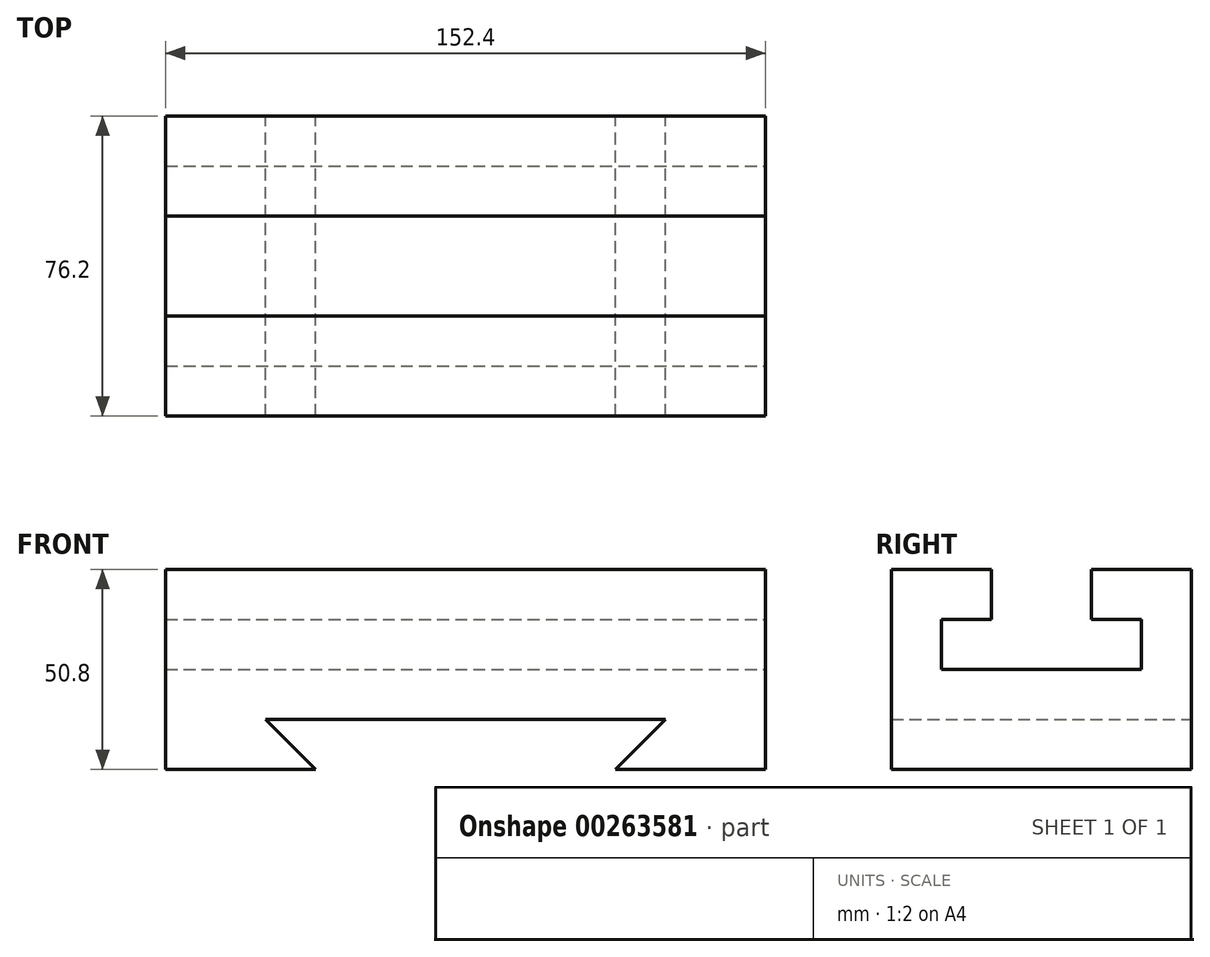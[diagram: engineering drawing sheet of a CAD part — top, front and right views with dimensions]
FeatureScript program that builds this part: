
annotation { "Feature Type Name" : "Feature", "Feature Type Description" : "" }
export const myFeature = defineFeature(function(context is Context, id is Id, definition is map)
    precondition{}
    {
        {
            var Q0;
            Q0=qCreatedBy(makeId("Front.planeOp"),FACE);
            var sketch = newSketch(context, id + "F0", { "sketchPlane" : qUnion([Q0])});
            skLineSegment(sketch, "E0.bottom", {"start": v(0, 0) * mm, "end": v(25.4, 0) * mm});
            skLineSegment(sketch, "E0.top", {"start": v(0, 50.8) * mm, "end": v(25.4, 50.8) * mm});
            skLineSegment(sketch, "E0.left", {"start": v(0, 0) * mm, "end": v(0, 50.8) * mm});
            skLineSegment(sketch, "E1.bottom", {"start": v(25.4, 50.8) * mm, "end": v(127, 50.8) * mm});
            skLineSegment(sketch, "E1.top", {"start": v(25.4, 12.7) * mm, "end": v(127, 12.7) * mm});
            skLineSegment(sketch, "E2.bottom", {"start": v(127, 50.8) * mm, "end": v(152.4, 50.8) * mm});
            skLineSegment(sketch, "E2.top", {"start": v(127, 0) * mm, "end": v(152.4, 0) * mm});
            skLineSegment(sketch, "E2.right", {"start": v(152.4, 50.8) * mm, "end": v(152.4, 0) * mm});
            skLineSegment(sketch, "E3", {"start": v(25.4, 12.7) * mm, "end": v(38.1, 0) * mm});
            skLineSegment(sketch, "E4", {"start": v(38.1, 0) * mm, "end": v(25.4, 0) * mm});
            skLineSegment(sketch, "E5", {"start": v(127, 0) * mm, "end": v(114.3, 0) * mm});
            skLineSegment(sketch, "E6", {"start": v(114.3, 0) * mm, "end": v(127, 12.7) * mm});
            skLineSegment(sketch, "E7", {"start": v(152.4, 50.8) * mm, "end": v(152.4, 38.1) * mm});
            skLineSegment(sketch, "E8", {"start": v(0, 38.1) * mm, "end": v(0, 50.8) * mm});
            skPoint(sketch, "E9.end.orphan", {"position": v(127, 0) * mm});
            skSolve(sketch);
        }
        {
            var Q0;
            {var subQ0=sQuery(id+"F0.wireOp",EDGE,"E0.top");Q0=makeQuery(id+"F0.imprint","IMPRINT",FACE,{"disambiguationData":[TD([[makeQuery(id+"F0.imprint","IMPRINT",EDGE,{"derivedFrom":subQ0}),-1.0]])]});}
            extrude(context, id + "F1", {"entities" : qUnion([Q0]), "depth" : 76.2 * mm});
        }
        {
            var Q0;
            Q0=makeQuery(id+"F1.opExtrude","SWEPT_FACE",FACE,{"disambiguationData":[OSD([sQuery(id+"F0.wireOp",EDGE,"E2.right"),sQuery(id+"F0.wireOp",EDGE,"E7")])]});
            var sketch = newSketch(context, id + "F2", { "sketchPlane" : qUnion([Q0])});
            skLineSegment(sketch, "E10", {"start": v(-76.2, 50.8) * mm, "end": v(-50.8, 50.8) * mm});
            skLineSegment(sketch, "E11", {"start": v(-50.8, 50.8) * mm, "end": v(-50.8, 38.1) * mm});
            skLineSegment(sketch, "E12", {"start": v(-50.8, 38.1) * mm, "end": v(-63.5, 38.1) * mm});
            skLineSegment(sketch, "E13", {"start": v(-63.5, 38.1) * mm, "end": v(-63.5, 25.4) * mm});
            skLineSegment(sketch, "E14", {"start": v(-63.5, 25.4) * mm, "end": v(-12.7, 25.4) * mm});
            skLineSegment(sketch, "E15", {"start": v(-12.7, 25.4) * mm, "end": v(-12.7, 38.1) * mm});
            skLineSegment(sketch, "E16", {"start": v(-12.7, 38.1) * mm, "end": v(-25.4, 38.1) * mm});
            skLineSegment(sketch, "E17", {"start": v(-25.4, 38.1) * mm, "end": v(-25.4, 50.8) * mm});
            skLineSegment(sketch, "E18", {"start": v(-25.4, 50.8) * mm, "end": v(0, 50.8) * mm});
            skSolve(sketch);
        }
        {
            var Q0;
            {var subQ0=sQuery(id+"F2.wireOp",EDGE,"E11");Q0=makeQuery(id+"F2.imprint","IMPRINT",FACE,{"disambiguationData":[TD([[makeQuery(id+"F2.imprint","IMPRINT",EDGE,{"derivedFrom":subQ0}),1.0]])]});}
            extrude(context, id + "F3", {"entities" : qUnion([Q0]), "operationType" : NewBodyOperationType.REMOVE, "oppositeDirection" : true, "depth" : 152.4 * mm});
        }
    });
